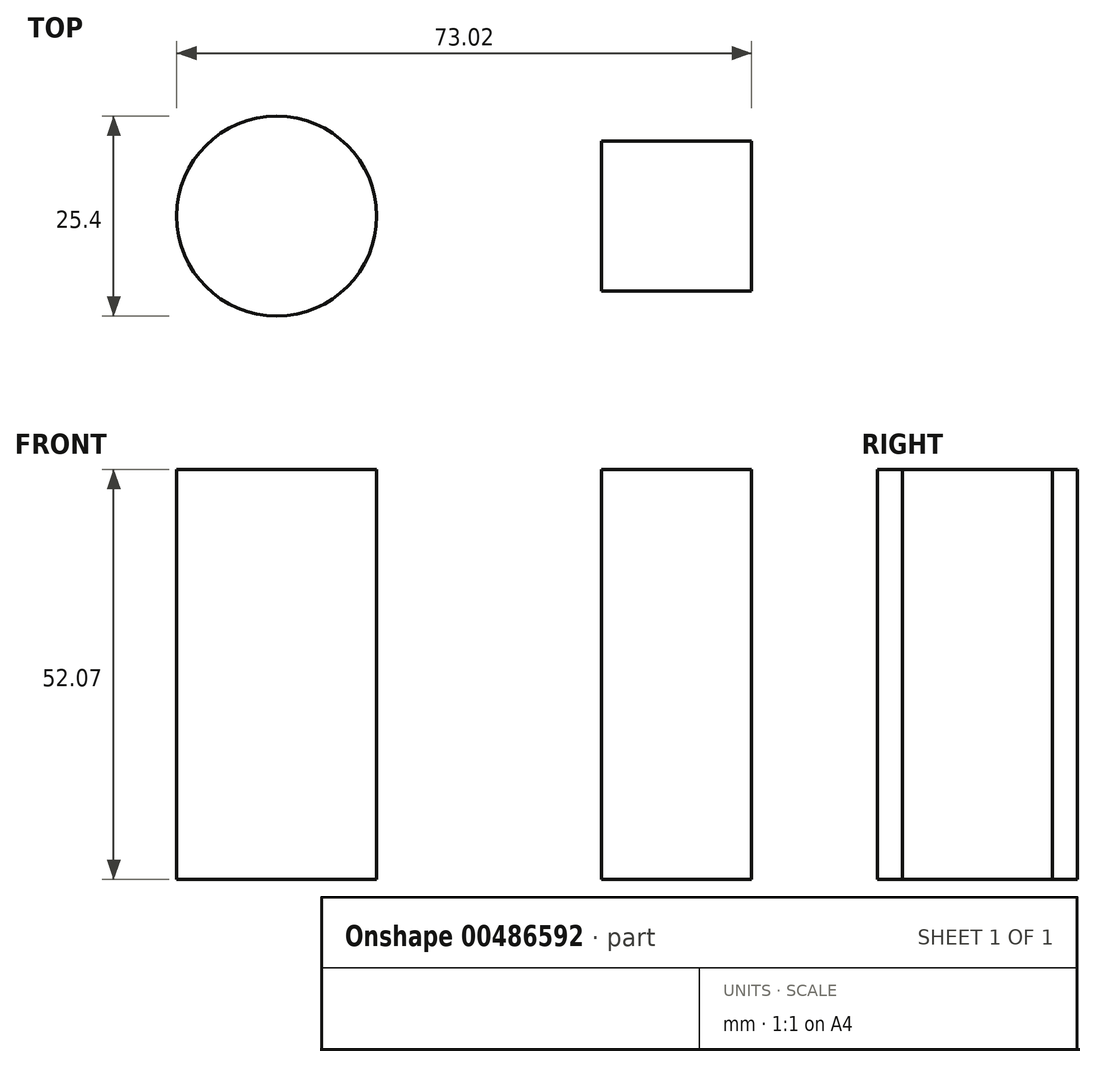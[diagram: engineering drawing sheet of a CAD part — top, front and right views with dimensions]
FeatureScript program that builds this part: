
annotation { "Feature Type Name" : "Feature", "Feature Type Description" : "" }
export const myFeature = defineFeature(function(context is Context, id is Id, definition is map)
    precondition{}
    {
        {
            var Q0;
            Q0=qCreatedBy(makeId("Top.planeOp"),FACE);
            var sketch = newSketch(context, id + "F0", { "sketchPlane" : qUnion([Q0])});
            skPoint(sketch, "E0", {"position": v(-31.75, 0) * mm});
            skPoint(sketch, "E1", {"position": v(-82.55, 0) * mm});
            skCircle(sketch, "E2", {"center": v(-82.55, 0) * mm, "radius": 12.7 * mm});
            skLineSegment(sketch, "E3.bottom", {"start": v(-22.22, 9.53) * mm, "end": v(-41.27, 9.53) * mm});
            skLineSegment(sketch, "E3.top", {"start": v(-22.22, -9.52) * mm, "end": v(-41.27, -9.52) * mm});
            skLineSegment(sketch, "E3.left", {"start": v(-22.22, 9.53) * mm, "end": v(-22.22, -9.52) * mm});
            skLineSegment(sketch, "E3.right", {"start": v(-41.27, 9.53) * mm, "end": v(-41.27, -9.52) * mm});
            skSolve(sketch);
        }
        {
            var Q0;
            Q0=makeQuery(id+"F0.imprint","IMPRINT",FACE,{"disambiguationData":[TD([[makeQuery(id+"F0.imprint","IMPRINT",EDGE,{"derivedFrom":sQuery(id+"F0.wireOp",EDGE,"E2")}),1.0]])]});
            var Q1;
            Q1=makeQuery(id+"F0.imprint","IMPRINT",FACE,{"disambiguationData":[TD([[makeQuery(id+"F0.imprint","IMPRINT",EDGE,{"derivedFrom":sQuery(id+"F0.wireOp",EDGE,"E3.bottom")}),1.0]])]});
            extrude(context, id + "F1", {"entities" : qUnion([Q0, Q1]), "depth" : 52.07 * mm});
        }
    });
